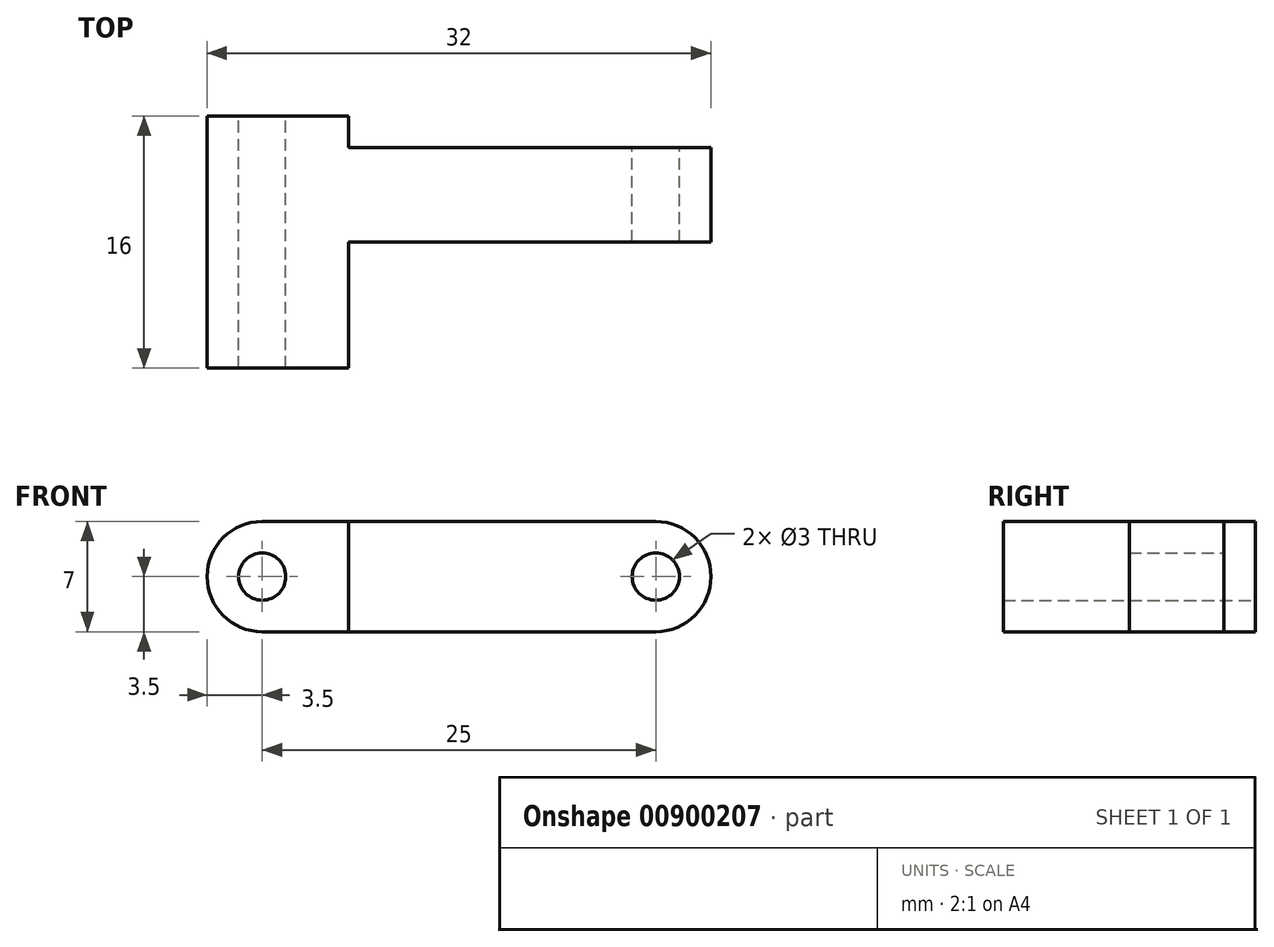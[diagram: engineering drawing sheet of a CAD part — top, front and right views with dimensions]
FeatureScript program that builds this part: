
annotation { "Feature Type Name" : "Feature", "Feature Type Description" : "" }
export const myFeature = defineFeature(function(context is Context, id is Id, definition is map)
    precondition{}
    {
        {
            var Q0;
            Q0=qCreatedBy(makeId("Front.planeOp"),FACE);
            var sketch = newSketch(context, id + "F0", { "sketchPlane" : qUnion([Q0])});
            skLineSegment(sketch, "E0", {"start": v(-12.5, 0) * mm, "end": v(12.5, 0) * mm});
            skArc(sketch, "E1", {"start": v(-12.5, 3.5) * mm, "mid": v(-16, 0) * mm, "end": v(-12.5, -3.5) * mm});
            skArc(sketch, "E2", {"start": v(12.5, -3.5) * mm, "mid": v(16, 0) * mm, "end": v(12.5, 3.5) * mm});
            skLineSegment(sketch, "E3", {"start": v(12.5, 3.5) * mm, "end": v(-12.5, 3.5) * mm});
            skLineSegment(sketch, "E4", {"start": v(-12.5, -3.5) * mm, "end": v(12.5, -3.5) * mm});
            skCircle(sketch, "E5", {"center": v(-12.5, 0) * mm, "radius": 1.5 * mm});
            skCircle(sketch, "E6", {"center": v(12.5, 0) * mm, "radius": 1.5 * mm});
            skSolve(sketch);
        }
        {
            var Q0;
            Q0 = qSketchRegion(id + "F0", true);
            extrude(context, id + "F1", {"entities" : qUnion([Q0]), "endBound" : BoundingType.SYMMETRIC, "depth" : 16 * mm, "offsetDistance" : 25.4 * mm});
        }
        {
            var Q0;
            Q0=makeQuery(id+"F1.opExtrude","SWEPT_FACE",FACE,{"disambiguationData":[OSD([sQuery(id+"F0.wireOp",EDGE,"E3")])]});
            var sketch = newSketch(context, id + "F2", { "sketchPlane" : qUnion([Q0])});
            skLineSegment(sketch, "E7.bottom", {"start": v(33.74, 21.66) * mm, "end": v(-7, 21.66) * mm});
            skLineSegment(sketch, "E7.top", {"start": v(33.74, 6) * mm, "end": v(-7, 6) * mm});
            skLineSegment(sketch, "E7.left", {"start": v(33.74, 21.66) * mm, "end": v(33.74, 6) * mm});
            skLineSegment(sketch, "E7.right", {"start": v(-7, 21.66) * mm, "end": v(-7, 6) * mm});
            skLineSegment(sketch, "E8.bottom", {"start": v(38.29, -22.4) * mm, "end": v(-7, -22.4) * mm});
            skLineSegment(sketch, "E8.top", {"start": v(38.29, 0) * mm, "end": v(-7, 0) * mm});
            skLineSegment(sketch, "E8.left", {"start": v(38.29, -22.4) * mm, "end": v(38.29, 0) * mm});
            skLineSegment(sketch, "E8.right", {"start": v(-7, -22.4) * mm, "end": v(-7, 0) * mm});
            skSolve(sketch);
        }
        {
            var Q0;
            Q0 = qSketchRegion(id + "F2", true);
            extrude(context, id + "F3", {"entities" : qUnion([Q0]), "operationType" : NewBodyOperationType.REMOVE, "oppositeDirection" : true, "depth" : 25.4 * mm, "offsetDistance" : 25.4 * mm});
        }
    });
